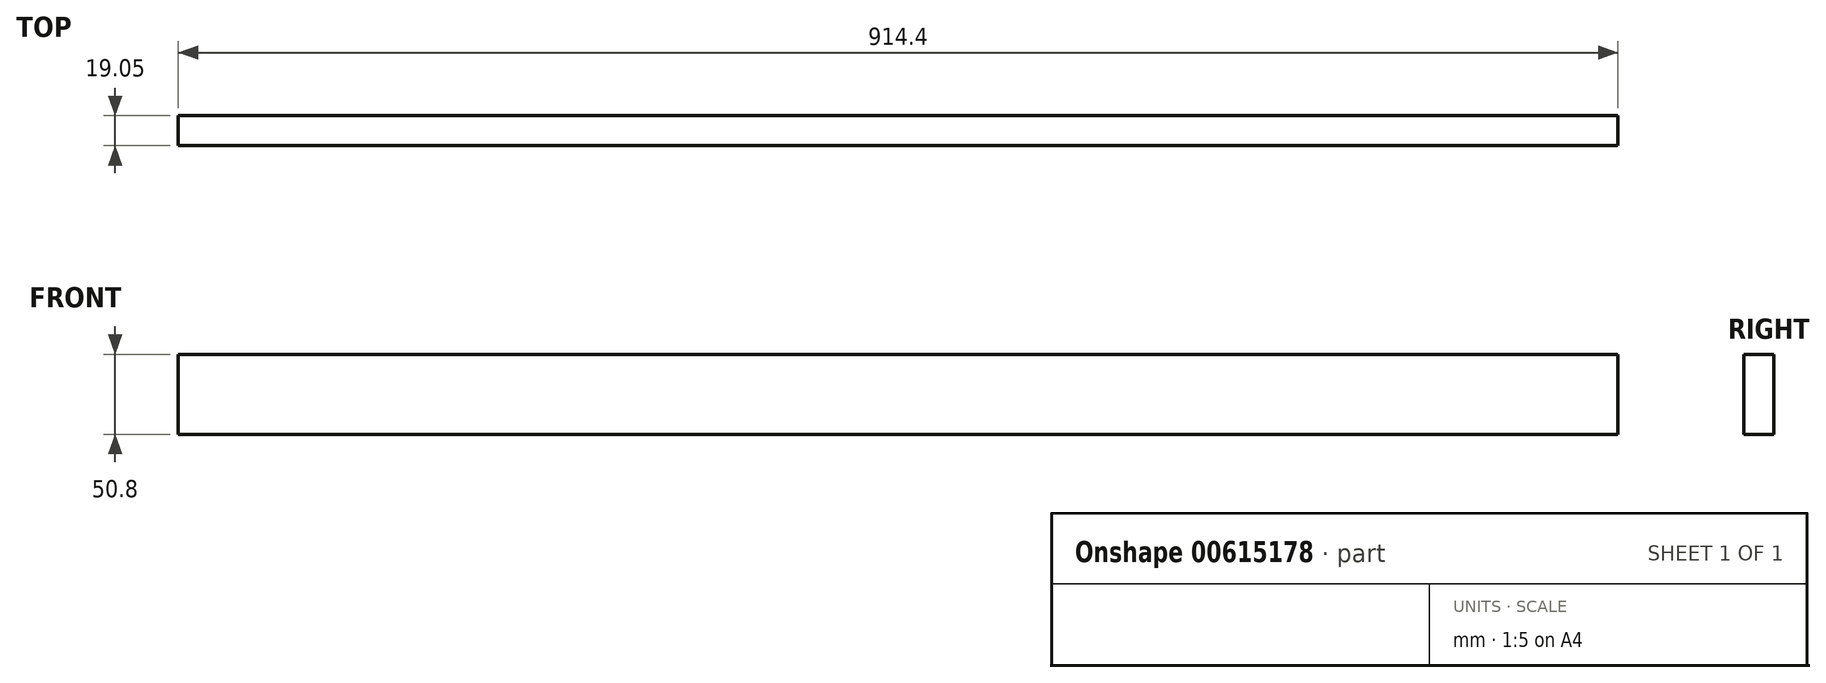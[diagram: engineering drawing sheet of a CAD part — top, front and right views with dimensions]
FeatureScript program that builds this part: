
annotation { "Feature Type Name" : "Feature", "Feature Type Description" : "" }
export const myFeature = defineFeature(function(context is Context, id is Id, definition is map)
    precondition{}
    {
        {
            var Q0;
            Q0=qCreatedBy(makeId("Front.planeOp"),FACE);
            var sketch = newSketch(context, id + "F0", { "sketchPlane" : qUnion([Q0])});
            skLineSegment(sketch, "E0.bottom", {"start": v(914.4, 50.8) * mm, "end": v(0, 50.8) * mm});
            skLineSegment(sketch, "E0.top", {"start": v(914.4, 0) * mm, "end": v(0, 0) * mm});
            skLineSegment(sketch, "E0.left", {"start": v(914.4, 50.8) * mm, "end": v(914.4, 0) * mm});
            skLineSegment(sketch, "E0.right", {"start": v(0, 50.8) * mm, "end": v(0, 0) * mm});
            skSolve(sketch);
        }
        {
            var Q0;
            Q0=makeQuery(id+"F0.imprint","IMPRINT",FACE,{"disambiguationData":[TD([[makeQuery(id+"F0.imprint","IMPRINT",EDGE,{"derivedFrom":sQuery(id+"F0.wireOp",EDGE,"E0.bottom")}),1.0]])]});
            extrude(context, id + "F1", {"entities" : qUnion([Q0]), "depth" : 19.05 * mm, "offsetDistance" : 25.4 * mm});
        }
    });
